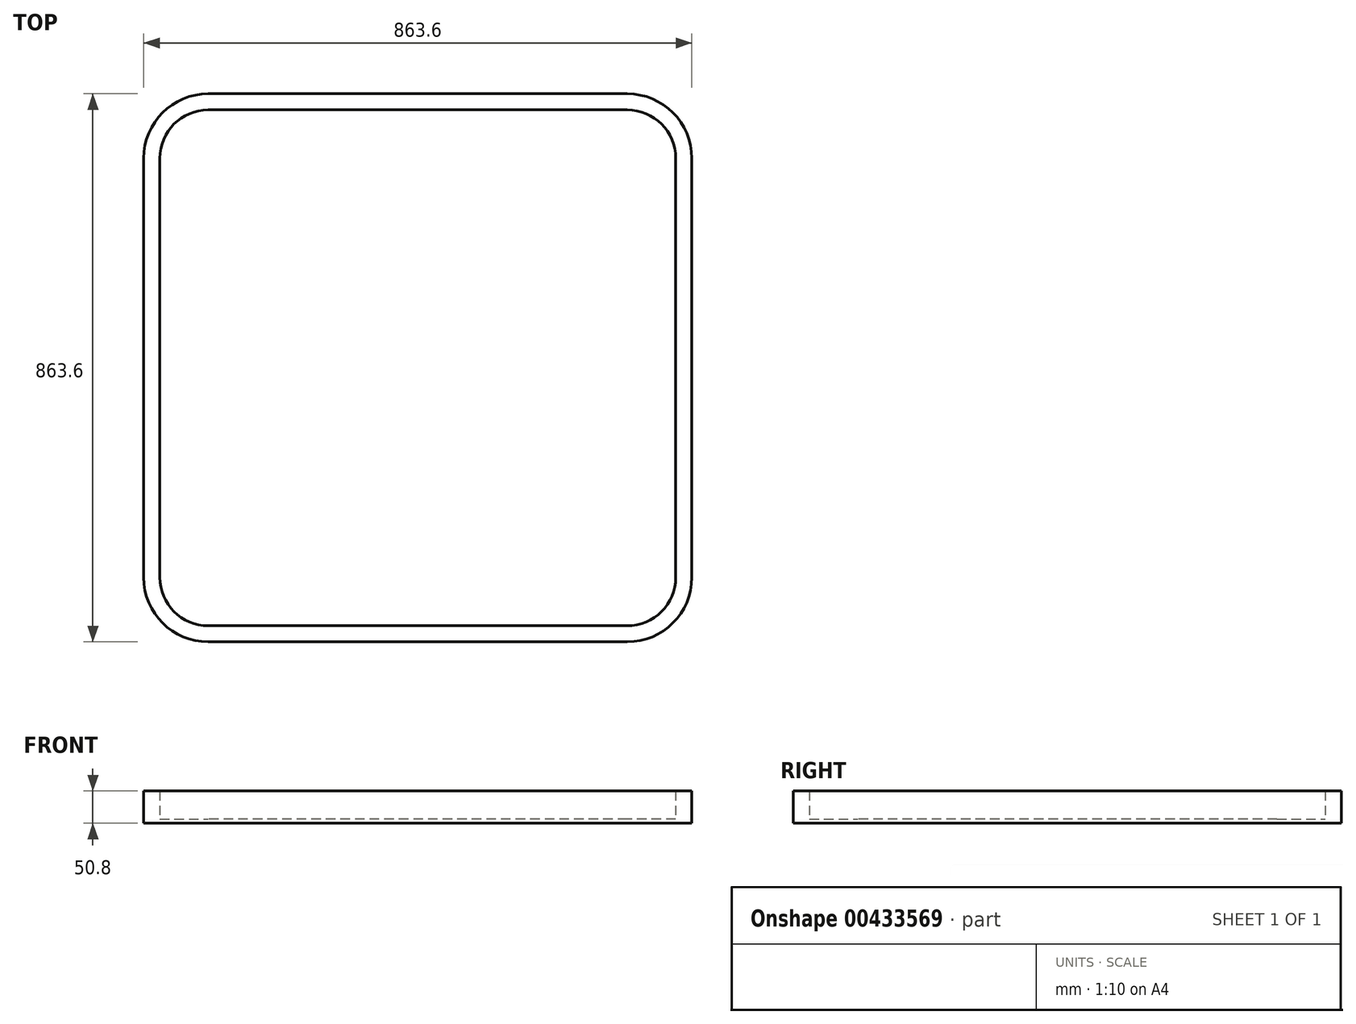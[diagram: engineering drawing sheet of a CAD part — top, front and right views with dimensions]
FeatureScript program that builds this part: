
annotation { "Feature Type Name" : "Feature", "Feature Type Description" : "" }
export const myFeature = defineFeature(function(context is Context, id is Id, definition is map)
    precondition{}
    {
        {
            var Q0;
            Q0=qCreatedBy(makeId("Top.planeOp"),FACE);
            var sketch = newSketch(context, id + "F0", { "sketchPlane" : qUnion([Q0])});
            skLineSegment(sketch, "E0.bottom", {"start": v(330.2, 431.8) * mm, "end": v(-330.2, 431.8) * mm});
            skLineSegment(sketch, "E0.top", {"start": v(330.2, -431.8) * mm, "end": v(-330.2, -431.8) * mm});
            skLineSegment(sketch, "E0.left", {"start": v(431.8, 330.2) * mm, "end": v(431.8, -330.2) * mm});
            skLineSegment(sketch, "E0.right", {"start": v(-431.8, 330.2) * mm, "end": v(-431.8, -330.2) * mm});
            skPoint(sketch, "E0.middle", {"position": v(0, 0) * mm});
            skPoint(sketch, "E1.visualSharp", {"position": v(-431.8, 431.8) * mm});
            skArc(sketch, "E1.filletArc", {"start": v(-330.2, 431.8) * mm, "mid": v(-402.04, 402.04) * mm, "end": v(-431.8, 330.2) * mm});
            skPoint(sketch, "E2.visualSharp", {"position": v(431.8, 431.8) * mm});
            skArc(sketch, "E2.filletArc", {"start": v(431.8, 330.2) * mm, "mid": v(402.04, 402.04) * mm, "end": v(330.2, 431.8) * mm});
            skPoint(sketch, "E3.visualSharp", {"position": v(431.8, -431.8) * mm});
            skArc(sketch, "E3.filletArc", {"start": v(330.2, -431.8) * mm, "mid": v(402.04, -402.04) * mm, "end": v(431.8, -330.2) * mm});
            skPoint(sketch, "E4.visualSharp", {"position": v(-431.8, -431.8) * mm});
            skArc(sketch, "E4.filletArc", {"start": v(-431.8, -330.2) * mm, "mid": v(-402.04, -402.04) * mm, "end": v(-330.2, -431.8) * mm});
            skLineSegment(sketch, "E5.0", {"start": v(406.4, 330.2) * mm, "end": v(406.4, -330.2) * mm});
            skArc(sketch, "E5.1", {"start": v(330.2, -406.4) * mm, "mid": v(384.08, -384.08) * mm, "end": v(406.4, -330.2) * mm});
            skArc(sketch, "E5.2", {"start": v(406.4, 330.2) * mm, "mid": v(384.08, 384.08) * mm, "end": v(330.2, 406.4) * mm});
            skLineSegment(sketch, "E5.3", {"start": v(330.2, -406.4) * mm, "end": v(-330.2, -406.4) * mm});
            skLineSegment(sketch, "E5.4", {"start": v(330.2, 406.4) * mm, "end": v(-330.2, 406.4) * mm});
            skArc(sketch, "E5.5", {"start": v(-330.2, 406.4) * mm, "mid": v(-384.08, 384.08) * mm, "end": v(-406.4, 330.2) * mm});
            skLineSegment(sketch, "E5.6", {"start": v(-406.4, 330.2) * mm, "end": v(-406.4, -330.2) * mm});
            skArc(sketch, "E5.7", {"start": v(-406.4, -330.2) * mm, "mid": v(-384.08, -384.08) * mm, "end": v(-330.2, -406.4) * mm});
            skSolve(sketch);
        }
        {
            var Q0;
            Q0 = qSketchRegion(id + "F0", true);
            extrude(context, id + "F1", {"entities" : qUnion([Q0]), "depth" : 50.8 * mm});
        }
        {
            var Q0;
            Q0=qCreatedBy(makeId("Top.planeOp"),FACE);
            var sketch = newSketch(context, id + "F2", { "sketchPlane" : qUnion([Q0])});
            skArc(sketch, "E6.0", {"start": v(-330.2, 406.4) * mm, "mid": v(-384.08, 384.08) * mm, "end": v(-406.4, 330.2) * mm});
            skLineSegment(sketch, "E6.1", {"start": v(330.2, 406.4) * mm, "end": v(-330.2, 406.4) * mm});
            skArc(sketch, "E6.2", {"start": v(406.4, 330.2) * mm, "mid": v(384.08, 384.08) * mm, "end": v(330.2, 406.4) * mm});
            skLineSegment(sketch, "E6.3", {"start": v(406.4, 330.2) * mm, "end": v(406.4, -330.2) * mm});
            skArc(sketch, "E6.4", {"start": v(330.2, -406.4) * mm, "mid": v(384.08, -384.08) * mm, "end": v(406.4, -330.2) * mm});
            skLineSegment(sketch, "E6.5", {"start": v(330.2, -406.4) * mm, "end": v(-330.2, -406.4) * mm});
            skArc(sketch, "E6.6", {"start": v(-406.4, -330.2) * mm, "mid": v(-384.08, -384.08) * mm, "end": v(-330.2, -406.4) * mm});
            skLineSegment(sketch, "E6.7", {"start": v(-406.4, 330.2) * mm, "end": v(-406.4, -330.2) * mm});
            skPoint(sketch, "E6.8", {"position": v(384.08, 384.08) * mm});
            skPoint(sketch, "E6.9", {"position": v(384.08, -384.08) * mm});
            skSolve(sketch);
        }
        {
            var Q0;
            Q0 = qSketchRegion(id + "F2", true);
            extrude(context, id + "F3", {"entities" : qUnion([Q0]), "operationType" : NewBodyOperationType.ADD, "depth" : 6.35 * mm});
        }
    });
